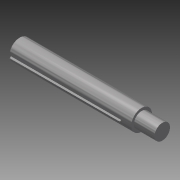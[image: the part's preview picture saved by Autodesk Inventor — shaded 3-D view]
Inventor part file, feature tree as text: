
AUTODESK INVENTOR PART (.ipt)
format: ipt  version: 2013 (Build 170138000, 138)  size: 111,104 bytes
history: native  units: in
note: dims shown in document units (in); Inventor stores cm internally (conversion verified against a paired STEP export)
features: extrude x4, sketch x3, fillet x1, chamfer x1, thread x1
ambient origin geometry x8: Origin, YZ Plane, XZ Plane, XY Plane, X Axis, Y Axis, Z Axis, Center Point
bodies: Solid1 (feature_tree)
feature tree (10):
  sketch  "Sketch1"  dims[d0=0.5in d2=0.0625in]
  extrude  "Extrusion1"  Depth=0.0625in
  extrude  "Extrusion2"  Depth=3.0in TaperAngle=0.0deg
  extrude  "Extrusion3"  Depth=0.5in TaperAngle=0.0deg
  fillet  "Fillet1"  Radius=2.75in
  chamfer  "Chamfer1"  Distance=0.0625in
  extrude  "Extrusion4"  Depth=0.05in TaperAngle=45.0deg
  thread  "Thread1"  [1 undecoded]
  sketch  "Sketch2"  dims[d3=0.125in d4=3.0in d5=0.0in]
  sketch  "Sketch3"  dims[d6=0.375in d8=0.5in d9=0.0in d10=2.75in d11=0.0in d12=0.0625in d13=0.05in d14=0.1in d15=45.0deg d16=0.185in d18=0.5in d19=0.0in d21=1.0in d22=0.0in]
note: 1 required parameter value undecoded (feature->parameter linkage not recoverable at this tier; creation-order binding heuristic only, values carry confidence <= 0.55)
